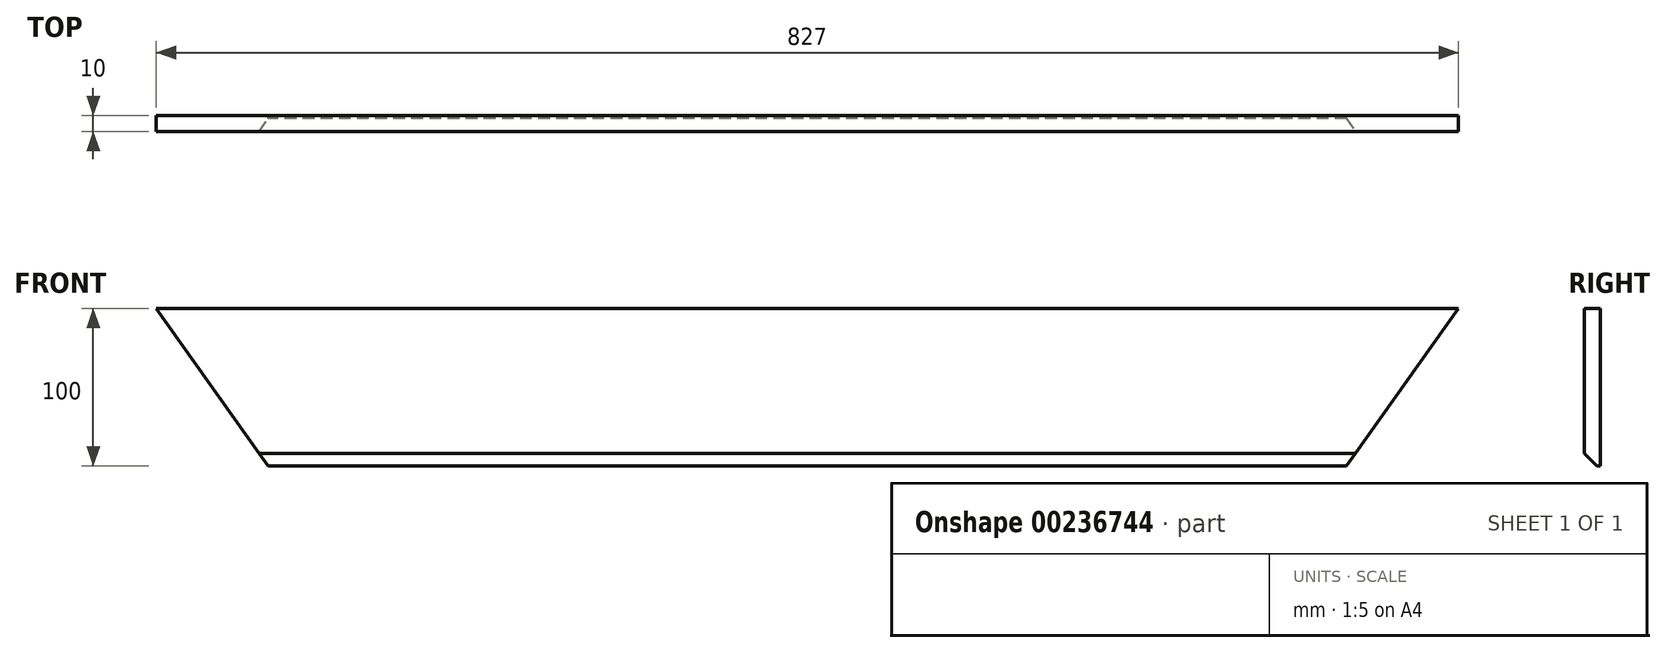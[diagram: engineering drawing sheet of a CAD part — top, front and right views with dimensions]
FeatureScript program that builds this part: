
annotation { "Feature Type Name" : "Feature", "Feature Type Description" : "" }
export const myFeature = defineFeature(function(context is Context, id is Id, definition is map)
    precondition{}
    {
        {
            var Q0;
            Q0=qCreatedBy(makeId("Front.planeOp"),FACE);
            var sketch = newSketch(context, id + "F0", { "sketchPlane" : qUnion([Q0])});
            skLineSegment(sketch, "E0", {"start": v(0, 0) * mm, "end": v(-71, 100) * mm});
            skLineSegment(sketch, "E1", {"start": v(-71, 100) * mm, "end": v(756, 100) * mm});
            skLineSegment(sketch, "E2", {"start": v(756, 100) * mm, "end": v(685, 0) * mm});
            skLineSegment(sketch, "E3", {"start": v(685, 0) * mm, "end": v(0, 0) * mm});
            skLineSegment(sketch, "E4", {"start": v(342.5, 100) * mm, "end": v(342.5, 0) * mm, "construction": true});
            skSolve(sketch);
        }
        {
            var Q0;
            Q0=makeQuery(id+"F0.imprint","IMPRINT",FACE,{"disambiguationData":[TD([[makeQuery(id+"F0.imprint","IMPRINT",EDGE,{"derivedFrom":sQuery(id+"F0.wireOp",EDGE,"E0")}),-1.0]])]});
            extrude(context, id + "F1", {"entities" : qUnion([Q0]), "depth" : 10 * mm, "offsetDistance" : 25 * mm});
        }
        {
            var Q0;
            Q0=makeQuery(id+"F1.opExtrude","SWEPT_FACE",FACE,{"disambiguationData":[OSD([sQuery(id+"F0.wireOp",EDGE,"E2")])]});
            var sketch = newSketch(context, id + "F2", { "sketchPlane" : qUnion([Q0])});
            skLineSegment(sketch, "E5", {"start": v(0, 519.2) * mm, "end": v(-15.18, 510.44) * mm});
            skLineSegment(sketch, "E6", {"start": v(-15.18, 510.44) * mm, "end": v(-15.18, 523.93) * mm});
            skLineSegment(sketch, "E7", {"start": v(-15.18, 523.93) * mm, "end": v(0, 523.93) * mm});
            skLineSegment(sketch, "E8", {"start": v(0, 523.93) * mm, "end": v(0, 519.2) * mm});
            skSolve(sketch);
        }
        {
            var Q0;
            {var subQ0=sQuery(id+"F2.wireOp",EDGE,"E6");Q0=makeQuery(id+"F2.imprint","IMPRINT",FACE,{"disambiguationData":[TD([[makeQuery(id+"F2.imprint","IMPRINT",EDGE,{"derivedFrom":subQ0}),-1.0]])]});}
            extrude(context, id + "F3", {"entities" : qUnion([Q0]), "operationType" : NewBodyOperationType.REMOVE, "endBound" : BoundingType.THROUGH_ALL, "oppositeDirection" : true, "depth" : 25 * mm, "offsetDistance" : 25 * mm});
        }
        {
            var Q0;
            Q0=makeQuery(id+"F1.opExtrude","SWEPT_FACE",FACE,{"disambiguationData":[OSD([sQuery(id+"F0.wireOp",EDGE,"E2")])]});
            var sketch = newSketch(context, id + "F4", { "sketchPlane" : qUnion([Q0])});
            skSolve(sketch);
        }
        {
            var Q0;
            {var subQ0=sQuery(id+"F0.wireOp",EDGE,"E2");Q0=makeQuery(id+"F4.imprint","IMPRINT",FACE,{"disambiguationData":[TD([[makeQuery(id+"F4.imprint","IMPRINT",EDGE,{"derivedFrom":makeQuery(id+"F1.opExtrude","CAP_EDGE",EDGE,{"disambiguationData":[OSD([subQ0])],"isStart":true})}),-1.0]])]});}
            var sketch = newSketch(context, id + "F5", { "sketchPlane" : qUnion([Q0])});
            skLineSegment(sketch, "E9", {"start": v(-210.87, 195.69) * mm, "end": v(-196.92, 209.65) * mm});
            skLineSegment(sketch, "E10", {"start": v(-196.92, 195.69) * mm, "end": v(-196.92, 209.65) * mm});
            skLineSegment(sketch, "E11", {"start": v(-210.87, 195.69) * mm, "end": v(-196.92, 195.69) * mm});
            skPoint(sketch, "E12.orphan", {"position": v(0, 406.56) * mm});
            skSolve(sketch);
        }
        {
            var Q0;
            Q0 = qSketchRegion(id + "F5", true);
            extrude(context, id + "F6", {"entities" : qUnion([Q0]), "operationType" : NewBodyOperationType.REMOVE, "endBound" : BoundingType.THROUGH_ALL, "oppositeDirection" : true, "depth" : 25 * mm, "offsetDistance" : 25 * mm});
        }
        {
            var Q0;
            Q0=makeQuery(id+"F1.opExtrude","CAP_EDGE",EDGE,{"disambiguationData":[OSD([sQuery(id+"F0.wireOp",EDGE,"E3")])],"isStart":false});
            chamfer(context, id + "F7", {"entities" : qUnion([Q0]), "chamferType" : ChamferType.OFFSET_ANGLE, "width" : 8 * mm, "oppositeDirection" : false, "angle" : 45 * degree, "tangentPropagation" : true});
        }
    });
